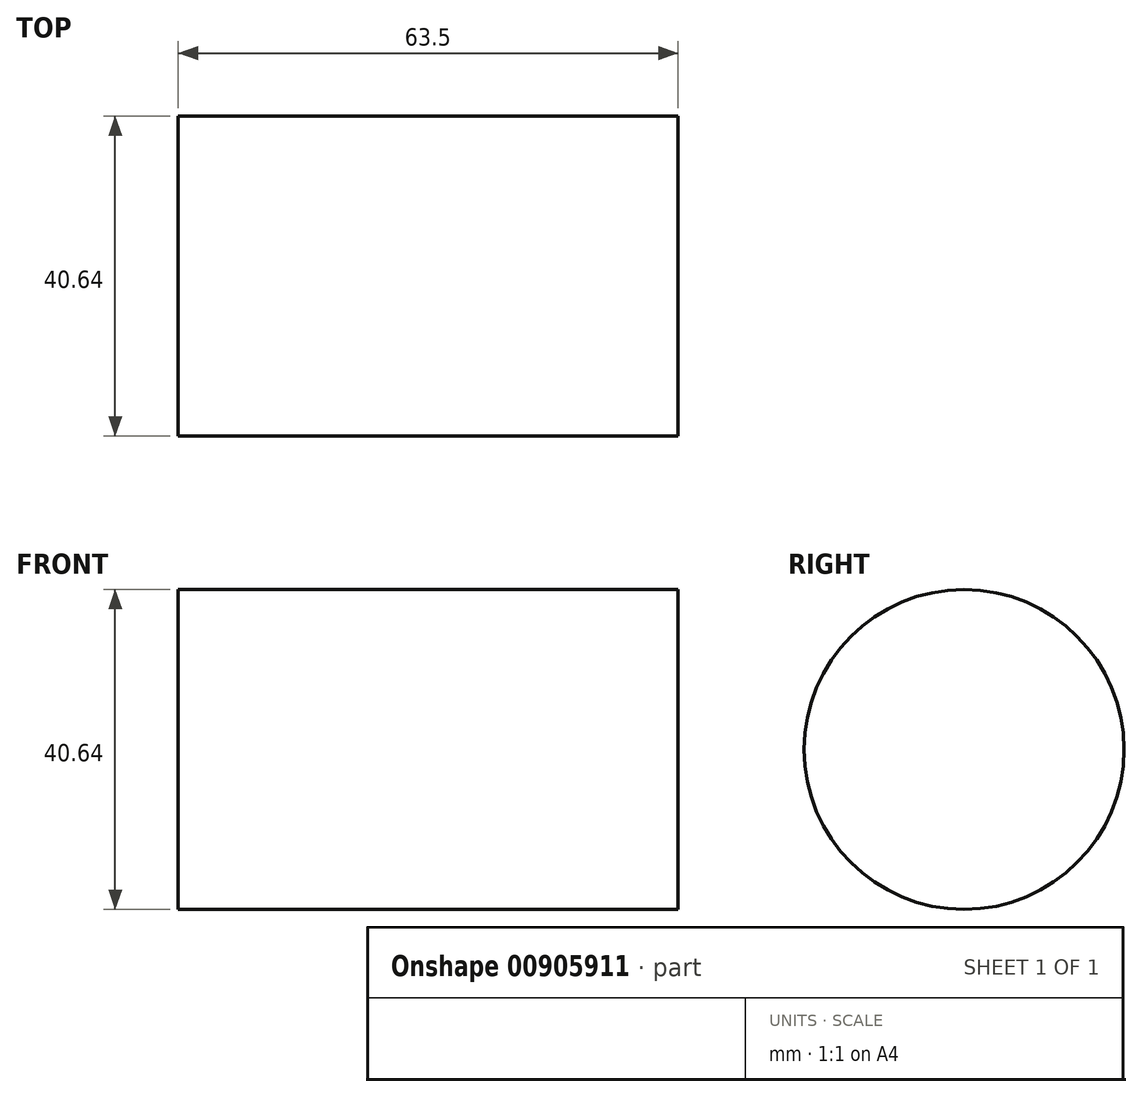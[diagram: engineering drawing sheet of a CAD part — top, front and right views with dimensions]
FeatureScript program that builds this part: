
annotation { "Feature Type Name" : "Feature", "Feature Type Description" : "" }
export const myFeature = defineFeature(function(context is Context, id is Id, definition is map)
    precondition{}
    {
        {
            var Q0;
            Q0=qCreatedBy(makeId("Right.planeOp"),FACE);
            var sketch = newSketch(context, id + "F0", { "sketchPlane" : qUnion([Q0])});
            skCircle(sketch, "E0", {"center": v(0, 0) * mm, "radius": 20.32 * mm});
            skSolve(sketch);
        }
        {
            var Q0;
            Q0 = qSketchRegion(id + "F0", true);
            extrude(context, id + "F1", {"entities" : qUnion([Q0]), "depth" : 63.5 * mm, "offsetDistance" : 25.4 * mm});
        }
    });
